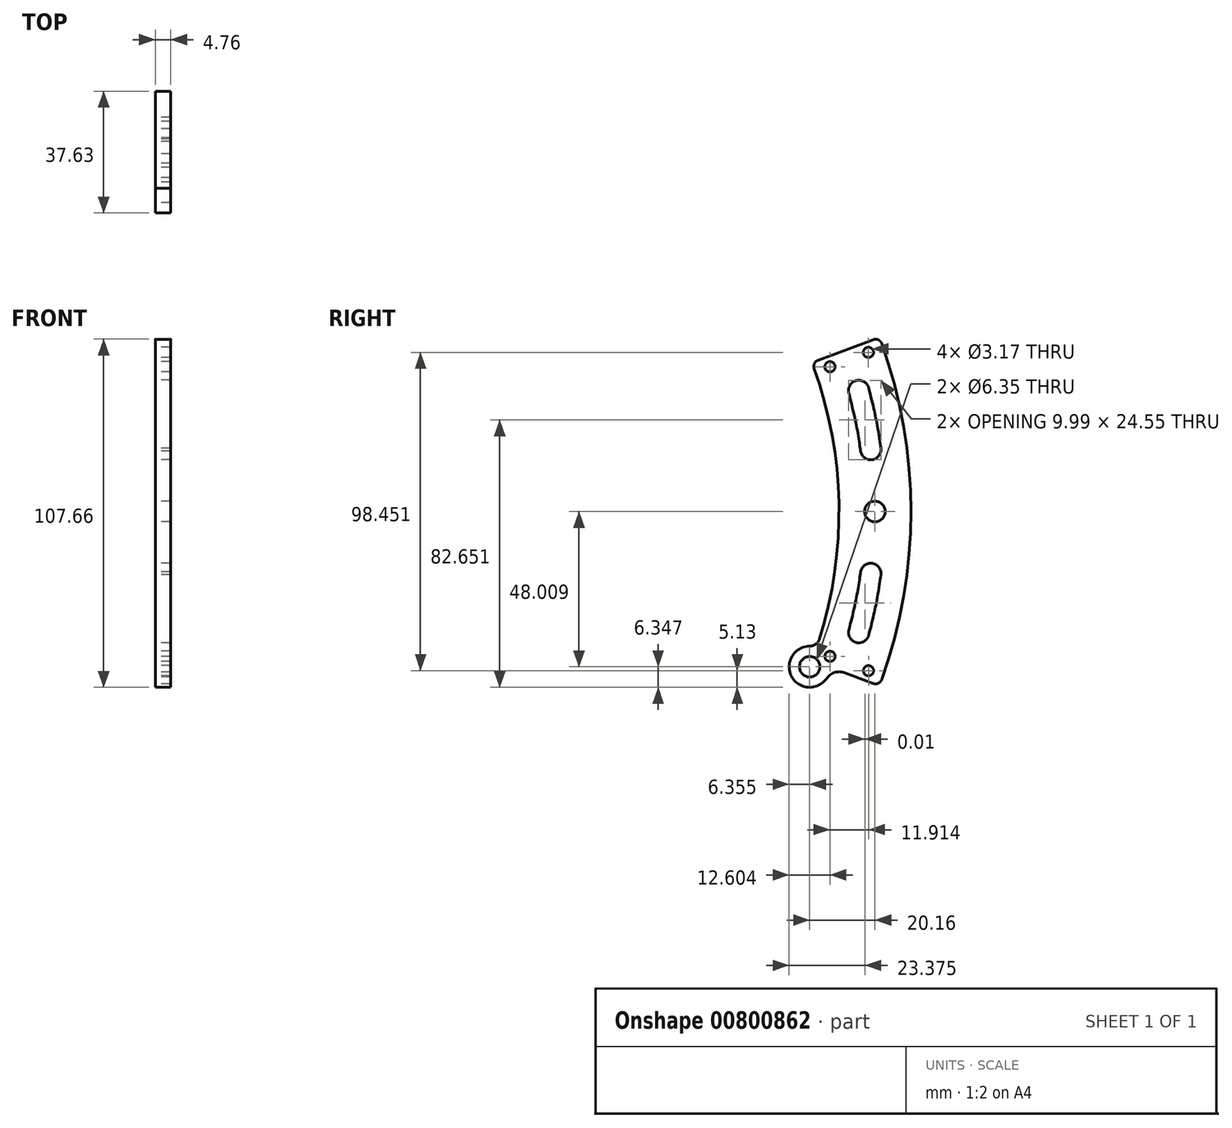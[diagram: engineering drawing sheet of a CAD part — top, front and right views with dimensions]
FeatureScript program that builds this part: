
annotation { "Feature Type Name" : "Feature", "Feature Type Description" : "" }
export const myFeature = defineFeature(function(context is Context, id is Id, definition is map)
    precondition{}
    {
        {
            var Q0;
            Q0=qCreatedBy(makeId("Right.planeOp"),FACE);
            var sketch = newSketch(context, id + "F0", { "sketchPlane" : qUnion([Q0])});
            skLineSegment(sketch, "E0", {"start": v(0, 0) * mm, "end": v(142.87, 0.03) * mm, "construction": true});
            skArc(sketch, "E1", {"start": v(124.1, 44.27) * mm, "mid": v(131.76, 1.2) * mm, "end": v(124.88, -42.02) * mm});
            skLineSegment(sketch, "E2", {"start": v(142.36, 53.2) * mm, "end": v(125.29, 46.82) * mm});
            skPoint(sketch, "E3.orphan", {"position": v(0, 131.76) * mm});
            skPoint(sketch, "E4.orphan", {"position": v(0, 142.88) * mm});
            skPoint(sketch, "E5.orphan", {"position": v(0, 153.99) * mm});
            skLineSegment(sketch, "E6.MirrorCS", {"start": v(142.38, -53.15) * mm, "end": v(133.52, -49.84) * mm});
            skPoint(sketch, "E7.orphan", {"position": v(0, -131.76) * mm});
            skPoint(sketch, "E8.orphan", {"position": v(0, -142.88) * mm});
            skPoint(sketch, "E9.orphan", {"position": v(0, -147.64) * mm});
            skPoint(sketch, "E10.orphan", {"position": v(0, -153.99) * mm});
            skPoint(sketch, "E11.trimOffspring.end.orphan", {"position": v(125.66, -40.14) * mm});
            skPoint(sketch, "E12.orphan", {"position": v(125.64, 40.18) * mm});
            skArc(sketch, "E13", {"start": v(108.51, -39.1) * mm, "mid": v(118.29, -45.87) * mm, "end": v(129.35, -50.26) * mm, "construction": true});
            skArc(sketch, "E14", {"start": v(131.2, -12.2) * mm, "mid": v(129.18, -25.95) * mm, "end": v(125.73, -39.4) * mm, "construction": true});
            skCircle(sketch, "E15", {"center": v(122.71, -47.98) * mm, "radius": 3.18 * mm});
            skArc(sketch, "E16", {"start": v(122.7, -41.63) * mm, "mid": v(117.1, -50.94) * mm, "end": v(127.94, -51.6) * mm});
            skArc(sketch, "E17.trimOffspring", {"start": v(123.44, -46.08) * mm, "mid": v(120.46, -53.4) * mm, "end": v(117.04, -60.53) * mm, "construction": true});
            skPoint(sketch, "E18.visualSharp", {"position": v(124.88, -42.02) * mm});
            skArc(sketch, "E18.filletArc", {"start": v(122.7, -41.63) * mm, "mid": v(124.58, -41.02) * mm, "end": v(125.73, -39.4) * mm});
            skPoint(sketch, "E19.visualSharp", {"position": v(129.06, -48.18) * mm});
            skArc(sketch, "E19.filletArc", {"start": v(133.52, -49.84) * mm, "mid": v(130.43, -49.76) * mm, "end": v(127.94, -51.6) * mm});
            skLineSegment(sketch, "E20", {"start": v(134.37, 47.05) * mm, "end": v(134.69, 46.94) * mm, "construction": true});
            skPoint(sketch, "E21.orphan", {"position": v(148.05, 42.35) * mm});
            skCircle(sketch, "E22", {"center": v(128.96, 44.8) * mm, "radius": 1.59 * mm});
            skCircle(sketch, "E23", {"center": v(140.86, 49.25) * mm, "radius": 1.59 * mm});
            skCircle(sketch, "E24.MirrorC", {"center": v(128.98, -44.76) * mm, "radius": 1.59 * mm});
            skCircle(sketch, "E25.MirrorC", {"center": v(140.88, -49.2) * mm, "radius": 1.59 * mm});
            skCircle(sketch, "E26", {"center": v(142.87, 0.03) * mm, "radius": 3.18 * mm});
            skPoint(sketch, "E27.startSnap0", {"position": v(138.35, 25.02) * mm});
            skLineSegment(sketch, "E28", {"start": v(136.39, 36.9) * mm, "end": v(136.64, 36.99) * mm});
            skLineSegment(sketch, "E29", {"start": v(141.59, 19.13) * mm, "end": v(141.49, 19.1) * mm});
            skArc(sketch, "E30.trimOffspring", {"start": v(140.7, 12.98) * mm, "mid": v(140.76, 12.15) * mm, "end": v(140.83, 11.31) * mm, "construction": true});
            skLineSegment(sketch, "E31.trimOffspring", {"start": v(137.78, 37.42) * mm, "end": v(137.88, 37.45) * mm});
            skFitSpline(sketch, "E32.0", {"points": [v(134.8, 36.7) * mm, v(135.2, 35.03) * mm, v(136.02, 31.74) * mm, v(136.91, 27.83) * mm, v(137.47, 24.94) * mm, v(137.94, 22.12) * mm, v(138.24, 20.06) * mm, v(138.45, 18.67) * mm]});
            skFitSpline(sketch, "E33.0", {"points": [v(140.96, 38.22) * mm, v(141.17, 37.39) * mm, v(141.58, 35.73) * mm, v(142.18, 33.24) * mm, v(142.66, 31.2) * mm, v(143.01, 29.59) * mm, v(143.35, 28) * mm, v(143.72, 26.06) * mm, v(144.22, 23.09) * mm, v(144.53, 20.98) * mm, v(144.73, 19.59) * mm]});
            skArc(sketch, "E34", {"start": v(134.8, 36.7) * mm, "mid": v(137.11, 40.54) * mm, "end": v(140.96, 38.22) * mm});
            skArc(sketch, "E35", {"start": v(138.45, 18.67) * mm, "mid": v(142.04, 16.05) * mm, "end": v(144.73, 19.59) * mm});
            skLineSegment(sketch, "E36.MirrorCS", {"start": v(136.4, -36.84) * mm, "end": v(136.65, -36.94) * mm});
            skLineSegment(sketch, "E37.MirrorCS", {"start": v(137.8, -37.37) * mm, "end": v(137.9, -37.4) * mm});
            skLineSegment(sketch, "E38.MirrorCS", {"start": v(141.6, -19.08) * mm, "end": v(141.5, -19.06) * mm});
            skLineSegment(sketch, "E39.MirrorCS", {"start": v(138.36, -26.77) * mm, "end": v(140.28, -27.12) * mm, "construction": true});
            skArc(sketch, "E40.MirrorCS", {"start": v(134.8, -36.64) * mm, "mid": v(137.13, -40.49) * mm, "end": v(140.97, -38.17) * mm});
            skFitSpline(sketch, "E41.MirrorCS", {"points": [v(134.8, -36.64) * mm, v(135.22, -34.98) * mm, v(136.04, -31.69) * mm, v(136.92, -27.78) * mm, v(137.48, -24.89) * mm, v(137.95, -22.07) * mm, v(138.25, -20.01) * mm, v(138.45, -18.62) * mm]});
            skPoint(sketch, "E42.MirrorP", {"position": v(138.36, -24.97) * mm});
            skPoint(sketch, "E43.MirrorP", {"position": v(148.07, -42.3) * mm});
            skArc(sketch, "E44.MirrorCS", {"start": v(138.45, -18.62) * mm, "mid": v(142.04, -16) * mm, "end": v(144.74, -19.53) * mm});
            skFitSpline(sketch, "E45.0", {"points": [v(140.97, -38.17) * mm, v(141.18, -37.34) * mm, v(141.6, -35.68) * mm, v(142.2, -33.2) * mm, v(142.67, -31.15) * mm, v(143.02, -29.54) * mm, v(143.36, -27.94) * mm, v(143.73, -26) * mm, v(144.23, -23.04) * mm, v(144.54, -20.93) * mm, v(144.74, -19.53) * mm]});
            skLineSegment(sketch, "E46.trimOffspring", {"start": v(134.69, 46.94) * mm, "end": v(134.4, 46.84) * mm, "construction": true});
            skPoint(sketch, "E47.0.start.orphan", {"position": v(145.73, 47.68) * mm});
            skPoint(sketch, "E48.orphan", {"position": v(133.83, 50.01) * mm});
            skLineSegment(sketch, "E49.trimOffspring", {"start": v(134.44, 46.66) * mm, "end": v(134.4, 46.84) * mm, "construction": true});
            skLineSegment(sketch, "E50.trimOffspring", {"start": v(124.5, 43.14) * mm, "end": v(123.8, 42.87) * mm, "construction": true});
            skPoint(sketch, "E51.visualSharp", {"position": v(144.24, 53.9) * mm});
            skArc(sketch, "E51.filletArc", {"start": v(144.94, 52) * mm, "mid": v(143.9, 53.14) * mm, "end": v(142.36, 53.2) * mm});
            skPoint(sketch, "E52.visualSharp", {"position": v(123.43, 46.12) * mm});
            skArc(sketch, "E52.filletArc", {"start": v(125.29, 46.82) * mm, "mid": v(124.17, 45.79) * mm, "end": v(124.1, 44.27) * mm});
            skPoint(sketch, "E27.end.orphan", {"position": v(140.27, 27.17) * mm});
            skPoint(sketch, "E27.start.orphan", {"position": v(138.35, 26.82) * mm});
            skArc(sketch, "E53.trimOffspring", {"start": v(144.96, -51.95) * mm, "mid": v(153.99, 0.03) * mm, "end": v(144.94, 52) * mm});
            skPoint(sketch, "E54.MirrorCS.start.orphan", {"position": v(145.74, -47.63) * mm});
            skPoint(sketch, "E55.visualSharp", {"position": v(144.26, -53.85) * mm});
            skArc(sketch, "E55.filletArc", {"start": v(142.38, -53.15) * mm, "mid": v(143.92, -53.09) * mm, "end": v(144.96, -51.95) * mm});
            skSolve(sketch);
        }
        {
            var Q0;
            Q0=qSketchRegion(id+"F0",true);
            extrude(context, id + "F1", {"entities" : qUnion([Q0]), "depth" : 4.76 * mm, "offsetDistance" : 25 * mm});
        }
    });
